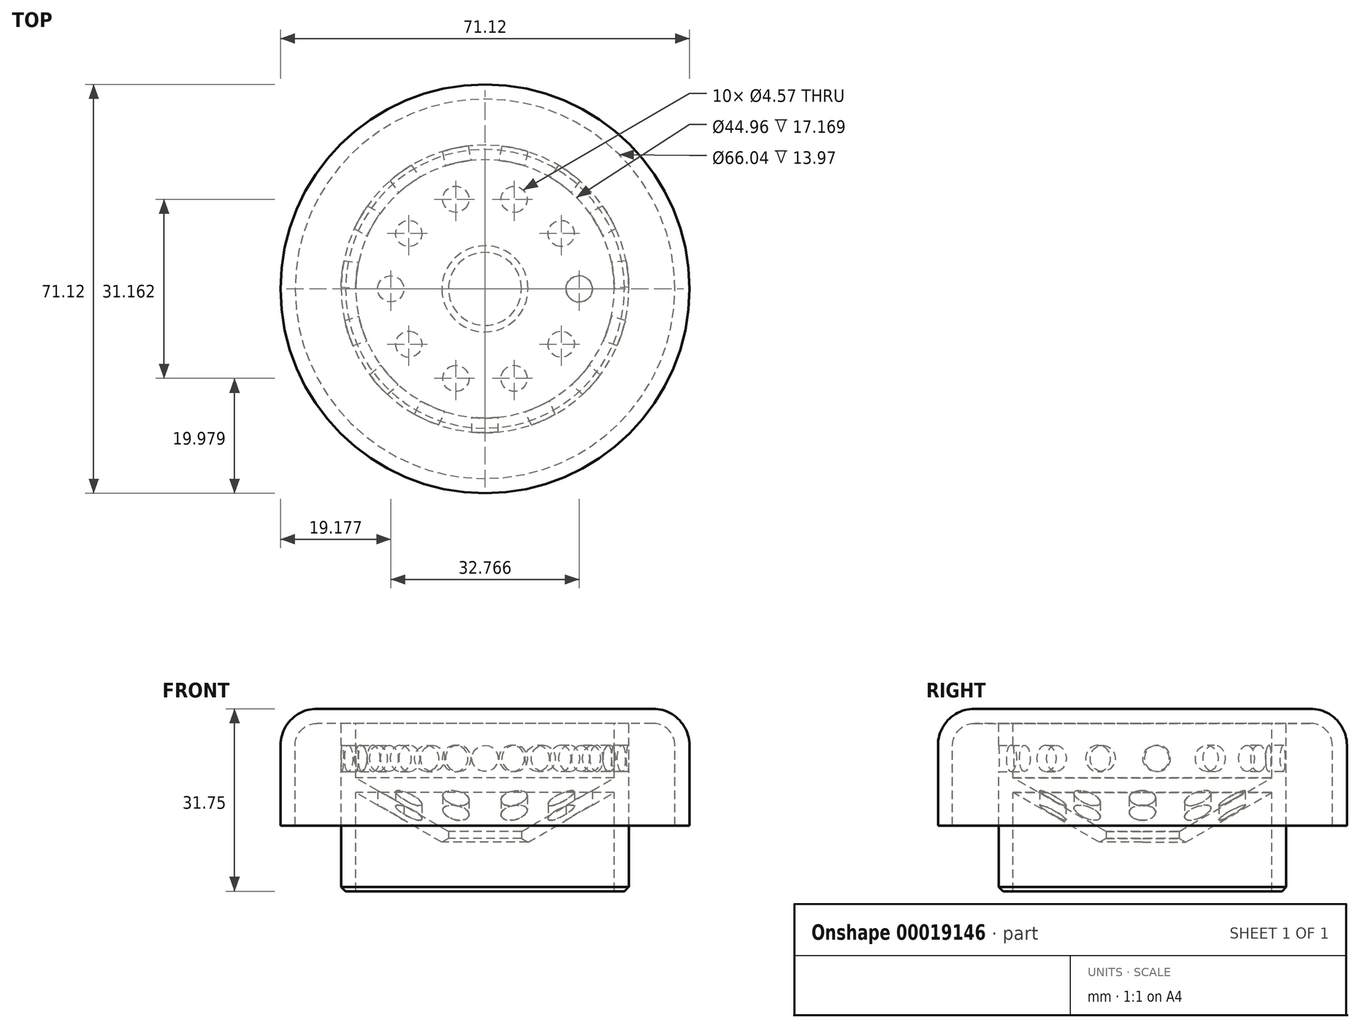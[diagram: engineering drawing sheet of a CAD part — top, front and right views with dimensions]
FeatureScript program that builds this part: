
annotation { "Feature Type Name" : "Feature", "Feature Type Description" : "" }
export const myFeature = defineFeature(function(context is Context, id is Id, definition is map)
    precondition{}
    {
        {
            var Q0;
            Q0=qCreatedBy(makeId("Front.planeOp"),FACE);
            var sketch = newSketch(context, id + "F0", { "sketchPlane" : qUnion([Q0])});
            skLineSegment(sketch, "E0", {"start": v(0, 48.66) * mm, "end": v(0, -20.5) * mm, "construction": true});
            skLineSegment(sketch, "E1", {"start": v(22.48, 0) * mm, "end": v(25.02, 0) * mm});
            skLineSegment(sketch, "E2", {"start": v(25.02, 0) * mm, "end": v(25.02, 29.21) * mm});
            skLineSegment(sketch, "E3", {"start": v(25.02, 29.21) * mm, "end": v(22.48, 29.21) * mm});
            skLineSegment(sketch, "E4", {"start": v(22.48, 29.21) * mm, "end": v(22.48, 0) * mm});
            skLineSegment(sketch, "E5", {"start": v(33.02, 11.43) * mm, "end": v(35.56, 11.43) * mm});
            skLineSegment(sketch, "E6", {"start": v(35.56, 11.43) * mm, "end": v(35.56, 31.75) * mm});
            skLineSegment(sketch, "E7", {"start": v(35.56, 31.75) * mm, "end": v(0, 31.75) * mm});
            skLineSegment(sketch, "E8", {"start": v(0, 31.75) * mm, "end": v(0, 29.21) * mm});
            skLineSegment(sketch, "E9", {"start": v(0, 29.21) * mm, "end": v(33.02, 29.21) * mm});
            skLineSegment(sketch, "E10", {"start": v(33.02, 29.21) * mm, "end": v(33.02, 11.43) * mm});
            skSolve(sketch);
        }
        {
            var Q0;
            Q0 = qSketchRegion(id + "F0", true);
            var Q1;
            Q1=sQuery(id+"F0.wireOp",EDGE,"E0");
            revolve(context, id + "F1", {"entities" : qUnion([Q0]), "axis" : qUnion([Q1]), "revolveType" : RevolveType.FULL});
        }
        {
            var Q0;
            Q0=qCreatedBy(makeId("Front.planeOp"),FACE);
            var sketch = newSketch(context, id + "F2", { "sketchPlane" : qUnion([Q0])});
            skCircle(sketch, "E11", {"center": v(0, 23.11) * mm, "radius": 2.29 * mm});
            skSolve(sketch);
        }
        {
            var Q0;
            Q0 = qSketchRegion(id + "F2", true);
            var Q1;
            Q1=makeQuery(id+"F1.opRevolve","SWEPT_FACE",FACE,{"disambiguationData":[OSD([sQuery(id+"F0.wireOp",EDGE,"E2")])]});
            var Q2;
            Q2=makeQuery(id+"F1.opRevolve","SWEPT_FACE",FACE,{"disambiguationData":[OSD([sQuery(id+"F0.wireOp",EDGE,"E2")])]});
            extrude(context, id + "F3", {"entities" : qUnion([Q0]), "operationType" : NewBodyOperationType.REMOVE, "endBound" : BoundingType.UP_TO_SURFACE, "endBoundEntityFace" : qUnion([Q1]), "depth" : 25.4 * mm});
        }
        {
            var Q0;
            Q0=makeQuery(id+"F3.boolean.opBoolean","COPY",FACE,{"disambiguationData":[OD(0.0)],"derivedFrom":makeQuery(id+"F3.opExtrude","SWEPT_FACE",FACE,{"disambiguationData":[OSD([sQuery(id+"F2.wireOp",EDGE,"E11")])]})});
            var Q1;
            Q1=makeQuery(id+"F1.opRevolve","SWEPT_FACE",FACE,{"disambiguationData":[OSD([sQuery(id+"F0.wireOp",EDGE,"E2")])]});
            circularPattern(context, id + "F4", {"faces" : qUnion([Q0]), "axis" : qUnion([Q1]), "angle" : 360 * degree, "instanceCount" : 15, "equalSpace" : true, "patternType" : PatternType.FACE});
        }
        {
            var Q0;
            Q0=qCreatedBy(makeId("Front.planeOp"),FACE);
            var sketch = newSketch(context, id + "F5", { "sketchPlane" : qUnion([Q0])});
            skLineSegment(sketch, "E12", {"start": v(0, 0) * mm, "end": v(0, 34.5) * mm, "construction": true});
            skLineSegment(sketch, "E13", {"start": v(0, 6.73) * mm, "end": v(22.48, 19.7) * mm});
            skLineSegment(sketch, "E14", {"start": v(22.48, 19.7) * mm, "end": v(22.48, 17.17) * mm});
            skLineSegment(sketch, "E15", {"start": v(22.48, 17.17) * mm, "end": v(0, 4.2) * mm});
            skLineSegment(sketch, "E16", {"start": v(0, 4.2) * mm, "end": v(0, 6.73) * mm});
            skLineSegment(sketch, "E17", {"start": v(40.44, 0) * mm, "end": v(0, 0) * mm, "construction": true});
            skSolve(sketch);
        }
        {
            var Q0;
            Q0 = qSketchRegion(id + "F5", true);
            var Q1;
            Q1=sQuery(id+"F5.wireOp",EDGE,"E12");
            revolve(context, id + "F6", {"operationType" : NewBodyOperationType.ADD, "entities" : qUnion([Q0]), "axis" : qUnion([Q1]), "revolveType" : RevolveType.FULL});
        }
        {
            var Q0;
            Q0=makeQuery(id+"F1.opRevolve","SWEPT_FACE",FACE,{"disambiguationData":[OSD([sQuery(id+"F0.wireOp",EDGE,"E1")])]});
            var sketch = newSketch(context, id + "F7", { "sketchPlane" : qUnion([Q0])});
            skCircle(sketch, "E18", {"center": v(16.38, 0) * mm, "radius": 2.29 * mm});
            skSolve(sketch);
        }
        {
            var Q0;
            Q0 = qSketchRegion(id + "F7", true);
            var Q1;
            {var subQ0=sQuery(id+"F0.wireOp",EDGE,"E9");Q1=makeQuery(id+"F1.opRevolve","SWEPT_FACE",FACE,{"disambiguationData":[OSD([subQ0]),TDD([makeQuery(id+"F0.imprint","IMPRINT",EDGE,{"disambiguationData":[TD([[makeQuery(id+"F0.imprint","INTERSECT",VERTEX,{"derivedFrom":[sQuery(id+"F0.wireOp",EDGE,"E4"),subQ0]}),1.0]])],"derivedFrom":subQ0})])]});}
            extrude(context, id + "F8", {"entities" : qUnion([Q0]), "operationType" : NewBodyOperationType.REMOVE, "endBound" : BoundingType.UP_TO_SURFACE, "oppositeDirection" : true, "endBoundEntityFace" : qUnion([Q1]), "depth" : 25.4 * mm});
        }
        {
            var Q0;
            Q0=makeQuery(id+"F8.boolean.opBoolean","COPY",FACE,{"derivedFrom":makeQuery(id+"F8.opExtrude","SWEPT_FACE",FACE,{"disambiguationData":[OSD([sQuery(id+"F7.wireOp",EDGE,"E18")])]})});
            var Q1;
            Q1=makeQuery(id+"F1.opRevolve","SWEPT_FACE",FACE,{"disambiguationData":[OSD([sQuery(id+"F0.wireOp",EDGE,"E2")])]});
            circularPattern(context, id + "F9", {"faces" : qUnion([Q0]), "axis" : qUnion([Q1]), "angle" : 360 * degree, "instanceCount" : 10, "equalSpace" : true, "patternType" : PatternType.FACE});
        }
        {
            var Q0;
            Q0=makeQuery(id+"F1.opRevolve","SWEPT_FACE",FACE,{"disambiguationData":[OSD([sQuery(id+"F0.wireOp",EDGE,"E1")])]});
            var sketch = newSketch(context, id + "F10", { "sketchPlane" : qUnion([Q0])});
            skCircle(sketch, "E19", {"center": v(0, 0) * mm, "radius": 6.35 * mm});
            skSolve(sketch);
        }
        {
            var Q0;
            Q0 = qSketchRegion(id + "F10", true);
            var Q1;
            {var subQ0=sQuery(id+"F0.wireOp",EDGE,"E9");Q1=makeQuery(id+"F1.opRevolve","SWEPT_FACE",FACE,{"disambiguationData":[OSD([subQ0]),TDD([makeQuery(id+"F0.imprint","IMPRINT",EDGE,{"disambiguationData":[TD([[makeQuery(id+"F0.imprint","INTERSECT",VERTEX,{"derivedFrom":[sQuery(id+"F0.wireOp",EDGE,"E8"),subQ0]}),-1.0]])],"derivedFrom":subQ0})])]});}
            extrude(context, id + "F11", {"entities" : qUnion([Q0]), "operationType" : NewBodyOperationType.REMOVE, "endBound" : BoundingType.UP_TO_SURFACE, "oppositeDirection" : true, "endBoundEntityFace" : qUnion([Q1]), "depth" : 25.4 * mm});
        }
        {
            var Q0;
            Q0=makeQuery(id+"F1.opRevolve","SWEPT_EDGE",EDGE,{"disambiguationData":[OSD([sQuery(id+"F0.wireOp",EDGE,"E6"),sQuery(id+"F0.wireOp",EDGE,"E7")])]});
            fillet(context, id + "F12", {"entities" : qUnion([Q0]), "radius" : 6.35 * mm, "tangentPropagation" : true, "allowEdgeOverflow" : false});
        }
        {
            var Q0;
            Q0=makeQuery(id+"F1.opRevolve","SWEPT_EDGE",EDGE,{"disambiguationData":[OSD([sQuery(id+"F0.wireOp",EDGE,"E9"),sQuery(id+"F0.wireOp",EDGE,"E10")])]});
            fillet(context, id + "F13", {"entities" : qUnion([Q0]), "radius" : 3.8 * mm, "tangentPropagation" : true, "allowEdgeOverflow" : false});
        }
        {
            var Q0;
            Q0=makeQuery(id+"F1.opRevolve","SWEPT_EDGE",EDGE,{"disambiguationData":[OSD([sQuery(id+"F0.wireOp",EDGE,"E1"),sQuery(id+"F0.wireOp",EDGE,"E2")])]});
            var Q1;
            Q1=makeQuery(id+"F11.boolean.opBoolean","INTERSECT",EDGE,{"derivedFrom":[makeQuery(id+"F6.opRevolve","SWEPT_FACE",FACE,{"disambiguationData":[OSD([sQuery(id+"F5.wireOp",EDGE,"E15")])]}),makeQuery(id+"F11.opExtrude","SWEPT_FACE",FACE,{"disambiguationData":[OSD([sQuery(id+"F10.wireOp",EDGE,"E19")])]})]});
            chamfer(context, id + "F14", {"entities" : qUnion([Q0, Q1]), "width" : 0.76 * mm, "tangentPropagation" : true});
        }
    });
